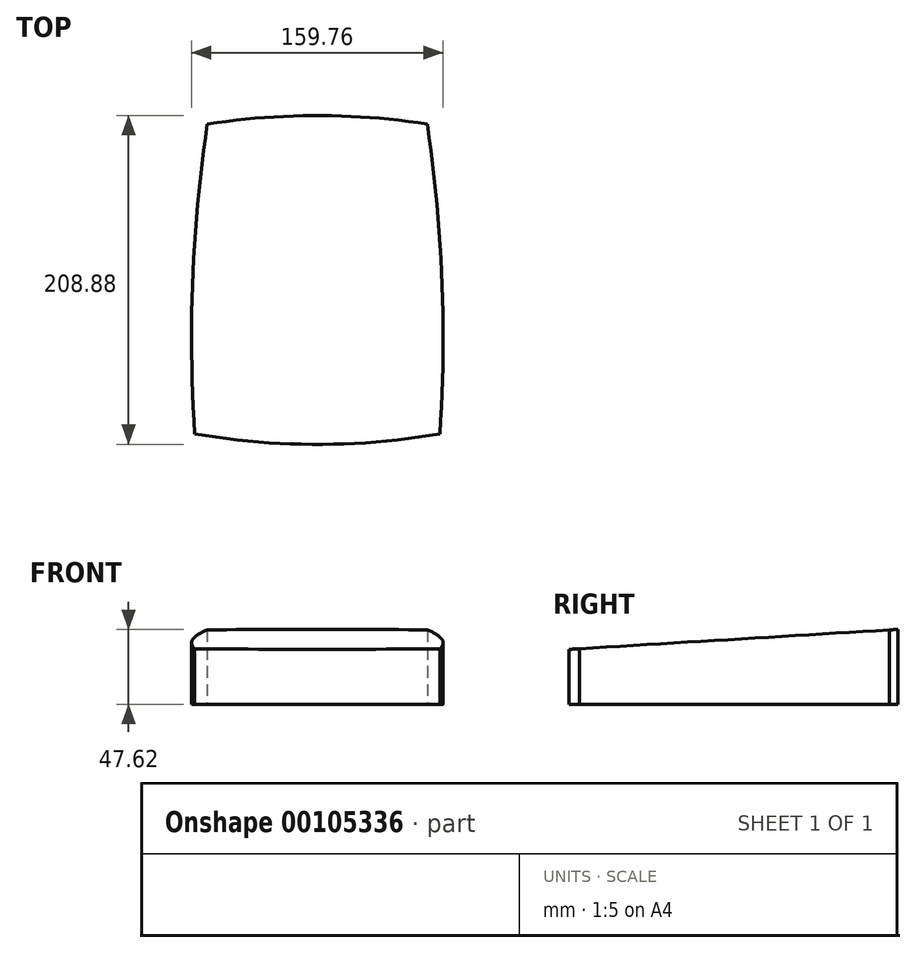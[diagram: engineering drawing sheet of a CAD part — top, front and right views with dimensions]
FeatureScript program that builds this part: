
annotation { "Feature Type Name" : "Feature", "Feature Type Description" : "" }
export const myFeature = defineFeature(function(context is Context, id is Id, definition is map)
    precondition{}
    {
        {
            var Q0;
            Q0=qCreatedBy(makeId("Top.planeOp"),FACE);
            var sketch = newSketch(context, id + "F0", { "sketchPlane" : qUnion([Q0])});
            skLineSegment(sketch, "E0", {"start": v(-69.85, 59.06) * mm, "end": v(-77.79, -137.8) * mm, "construction": true});
            skLineSegment(sketch, "E1", {"start": v(-77.79, -137.8) * mm, "end": v(77.79, -137.8) * mm, "construction": true});
            skLineSegment(sketch, "E2", {"start": v(77.79, -137.8) * mm, "end": v(69.85, 59.06) * mm, "construction": true});
            skLineSegment(sketch, "E3", {"start": v(69.85, 59.06) * mm, "end": v(-69.85, 59.06) * mm, "construction": true});
            skSolve(sketch);
        }
        {
            var Q0;
            Q0=qCreatedBy(makeId("Top.planeOp"),FACE);
            var sketch = newSketch(context, id + "F1", { "sketchPlane" : qUnion([Q0])});
            skArc(sketch, "E4", {"start": v(-69.85, 59.06) * mm, "mid": v(-79.14, -39.16) * mm, "end": v(-77.79, -137.8) * mm});
            skArc(sketch, "E5", {"start": v(69.85, 59.06) * mm, "mid": v(35.03, 63.08) * mm, "end": v(0, 64.42) * mm});
            skArc(sketch, "E6", {"start": v(77.79, -137.8) * mm, "mid": v(79.14, -39.16) * mm, "end": v(69.85, 59.06) * mm});
            skArc(sketch, "E7", {"start": v(-77.79, -137.8) * mm, "mid": v(-39.04, -142.8) * mm, "end": v(0, -144.46) * mm});
            skLineSegment(sketch, "E8", {"start": v(-77.79, -137.8) * mm, "end": v(-83.02, -60.54) * mm, "construction": true});
            skArc(sketch, "E9", {"start": v(0, 64.42) * mm, "mid": v(-35.03, 63.08) * mm, "end": v(-69.85, 59.06) * mm});
            skArc(sketch, "E10", {"start": v(0, -144.46) * mm, "mid": v(39.04, -142.8) * mm, "end": v(77.79, -137.8) * mm});
            skSolve(sketch);
        }
        {
            var Q0;
            Q0=qCreatedBy(makeId("Right.planeOp"),FACE);
            var sketch = newSketch(context, id + "F2", { "sketchPlane" : qUnion([Q0])});
            skLineSegment(sketch, "E11.bottom", {"start": v(-144.46, 0) * mm, "end": v(64.42, 0) * mm});
            skLineSegment(sketch, "E11.top", {"start": v(-144.46, 34.92) * mm, "end": v(-40.02, 41.28) * mm});
            skLineSegment(sketch, "E11.left", {"start": v(-144.46, 0) * mm, "end": v(-144.46, 34.93) * mm});
            skLineSegment(sketch, "E11.right", {"start": v(64.42, 0) * mm, "end": v(64.42, 47.63) * mm});
            skLineSegment(sketch, "E12", {"start": v(-40.02, 41.28) * mm, "end": v(64.42, 47.63) * mm});
            skSolve(sketch);
        }
        {
            var Q0;
            Q0 = qSketchRegion(id + "F2", true);
            extrude(context, id + "F3", {"entities" : qUnion([Q0]), "endBound" : BoundingType.SYMMETRIC, "depth" : 165.1 * mm});
        }
        {
            var Q0;
            Q0 = qSketchRegion(id + "F1", true);
            extrude(context, id + "F4", {"entities" : qUnion([Q0]), "operationType" : NewBodyOperationType.INTERSECT, "endBound" : BoundingType.THROUGH_ALL, "depth" : 25.4 * mm});
        }
    });
